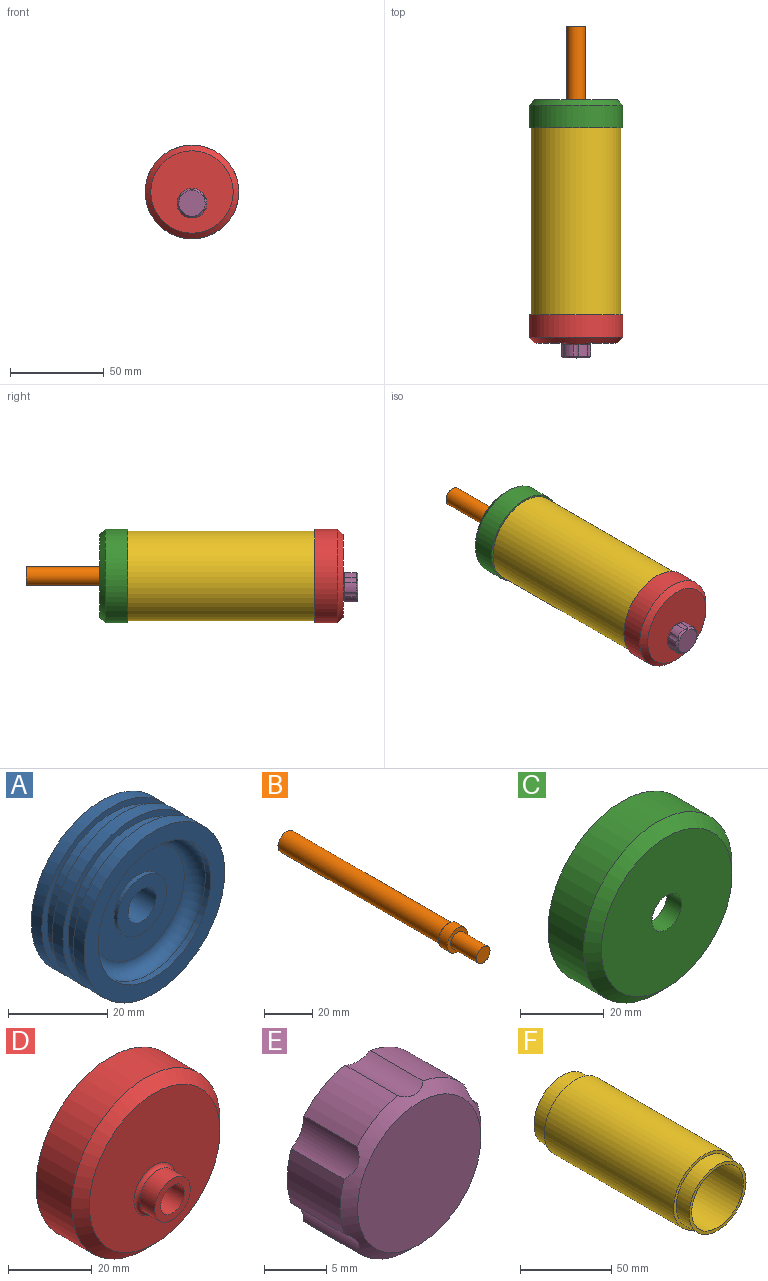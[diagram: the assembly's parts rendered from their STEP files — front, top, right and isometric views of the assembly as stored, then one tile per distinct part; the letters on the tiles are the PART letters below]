
ASSEMBLY  parts=6 mates=5
PART A: 22 faces, bbox 40x15.6x40 mm
  f0: cylinder r=20mm len=40mm, axis (0,1,0), area 377mm2, adj f6,f17
  f1: cylinder r=20mm len=40mm, axis (0,1,0), area 377mm2, adj f5,f15
  f2: cylinder r=7mm len=14mm, axis (0,1,0), area 44mm2, adj f3,f12
  f3: plane 26x26mm, normal (0,1,0), area 377mm2, adj f2,f20
  f4: cylinder r=16mm len=32mm, axis (0,1,0), area 150.8mm2, adj f5,f20
  f5: plane 40x40mm, normal (0,1,0), area 452.4mm2, adj f1,f4
  f6: plane 40x40mm, normal (0,-1,0), area 452.4mm2, adj f0,f7
  f7: cylinder r=16mm len=32mm, axis (0,1,0), area 150.8mm2, adj f6,f21
  f8: plane 26x26mm, normal (0,-1,0), area 377mm2, adj f9,f21
  f9: cylinder r=7mm len=14mm, axis (0,1,0), area 44mm2, adj f8,f10
  f10: plane 14x14mm, normal (0,-1,0), area 103.7mm2, adj f9,f11
  f11: cylinder r=4mm len=8mm, axis (0,1,0), area 201.1mm2, adj f10,f12
  f12: plane 14x14mm, normal (0,1,0), area 103.7mm2, adj f2,f11
  f13: plane 40x40mm, normal (0,1,0), area 181.4mm2, adj f14,f16
  f14: cylinder r=18.5mm len=37mm, axis (0,-1,0), area 348.7mm2, adj f13,f15
  f15: plane 40x40mm, normal (0,-1,0), area 181.4mm2, adj f1,f14
  f16: cylinder r=20mm len=40mm, axis (0,1,0), area 377mm2, adj f13,f19
  f17: plane 40x40mm, normal (0,1,0), area 181.4mm2, adj f0,f18
  f18: cylinder r=18.5mm len=37mm, axis (0,-1,0), area 348.7mm2, adj f17,f19
  f19: plane 40x40mm, normal (0,-1,0), area 181.4mm2, adj f16,f18
  f20: torus R=13mm, axis (0,1,0), area 441.5mm2, adj f3,f4
  f21: torus R=13mm, axis (0,1,0), area 441.5mm2, adj f7,f8
PART B: 7 faces, bbox 12x115x12 mm
  f0: plane 12x12mm, normal (0,-1,0), area 62.8mm2, adj f1,f3
  f1: cylinder r=4mm len=15mm, axis (0,1,0), area 377mm2, adj f0,f2
  f2: plane 8x8mm, normal (0,-1,0), area 50.3mm2, adj f1
  f3: cylinder r=6mm len=12mm, axis (0,-1,0), area 188.5mm2, adj f0,f6
  f4: plane 10x10mm, normal (0,1,0), area 78.5mm2, adj f5
  f5: cylinder r=5mm len=94mm, axis (0,1,0), area 2953.1mm2, adj f4,f6
  f6: cone r=6mm half-angle=45deg, axis (0,-1,0), area 48.9mm2, adj f3,f5
PART C: 7 faces, bbox 50x15x50 mm
  f0: plane 44x44mm, normal (0,-1,0), area 1442mm2, adj f1,f6
  f1: cylinder r=5mm len=10mm, axis (0,1,0), area 157.1mm2, adj f0,f2
  f2: plane 44x44mm, normal (0,1,0), area 1442mm2, adj f1,f3
  f3: cylinder r=22mm len=44mm, axis (0,1,0), area 1382.3mm2, adj f2,f4
  f4: plane 50x50mm, normal (0,1,0), area 443mm2, adj f3,f5
  f5: cylinder r=25mm len=50mm, axis (0,1,0), area 1885mm2, adj f4,f6
  f6: cone r=25mm half-angle=45deg, axis (0,1,0), area 626.4mm2, adj f0,f5
PART D: 10 faces, bbox 50x21x50 mm
  f0: plane 44x44mm, normal (0,1,0), area 1470.3mm2, adj f1,f8
  f1: cylinder r=22mm len=44mm, axis (0,1,0), area 1382.3mm2, adj f0,f2
  f2: plane 50x50mm, normal (0,1,0), area 443mm2, adj f1,f3
  f3: cylinder r=25mm len=50mm, axis (0,1,0), area 1885mm2, adj f2,f5
  f4: plane 44x44mm, normal (0,-1,0), area 1366.6mm2, adj f5,f9
  f5: cone r=25mm half-angle=45deg, axis (0,1,0), area 626.4mm2, adj f3,f4
  f6: cylinder r=6mm len=12mm, axis (0,1,0), area 188.5mm2, adj f7,f9
  f7: plane 12x12mm, normal (0,-1,0), area 62.8mm2, adj f6,f8
  f8: cylinder r=4mm len=11mm, axis (0,-1,0), area 276.5mm2, adj f0,f7
  f9: torus R=7mm, axis (0,1,0), area 62.8mm2, adj f4,f6
PART E: 17 faces, bbox 16x7x16 mm
  f0: cylinder r=8mm len=6mm, axis (0,1,0), area 32.9mm2, adj f7,f10,f11,f16
  f1: cylinder r=8mm len=6mm, axis (0,1,0), area 32.9mm2, adj f7,f10,f15,f16
  f2: cylinder r=8mm len=6mm, axis (0,1,0), area 32.9mm2, adj f7,f10,f14,f15
  f3: cylinder r=8mm len=6mm, axis (0,1,0), area 32.9mm2, adj f7,f10,f13,f14
  f4: cylinder r=8mm len=6mm, axis (0,1,0), area 32.9mm2, adj f7,f10,f12,f13
  f5: cylinder r=8mm len=6mm, axis (0,1,0), area 32.9mm2, adj f7,f10,f11,f12
  f6: plane 14x14mm, normal (0,-1,0), area 153.9mm2, adj f10
  f7: plane 16x15.74mm, normal (0,1,0), area 82.1mm2, adj f0,f1,f2,f3,f4,f5,f8,f11
  f8: cylinder r=6mm len=12mm, axis (0,1,0), area 188.5mm2, adj f7,f9
  f9: plane 12x12mm, normal (0,1,0), area 113.1mm2, adj f8
  f10: cone r=7mm half-angle=45deg, axis (0,1,0), area 58.4mm2, adj f0,f1,f2,f3,f4,f5,f6,f11
  f11: cylinder r=3mm len=6.5mm, axis (0,-1,0), area 19mm2, adj f0,f5,f7,f10
  f12: cylinder r=3mm len=6.5mm, axis (0,-1,0), area 19mm2, adj f4,f5,f7,f10
  f13: cylinder r=3mm len=6.5mm, axis (0,-1,0), area 19mm2, adj f3,f4,f7,f10
  f14: cylinder r=3mm len=6.5mm, axis (0,-1,0), area 19mm2, adj f2,f3,f7,f10
  f15: cylinder r=3mm len=6.5mm, axis (0,-1,0), area 19mm2, adj f1,f2,f7,f10
  f16: cylinder r=3mm len=6.5mm, axis (0,-1,0), area 19mm2, adj f0,f1,f7,f10
PART F: 8 faces, bbox 48x120x48 mm
  f0: cylinder r=22mm len=44mm, axis (0,1,0), area 1382.3mm2, adj f1,f7
  f1: plane 48x48mm, normal (0,1,0), area 289mm2, adj f0,f2
  f2: cylinder r=24mm len=100mm, axis (0,1,0), area 15079.6mm2, adj f1,f3
  f3: plane 48x48mm, normal (0,-1,0), area 289mm2, adj f2,f4
  f4: cylinder r=22mm len=44mm, axis (0,1,0), area 1382.3mm2, adj f3,f5
  f5: plane 44x44mm, normal (0,-1,0), area 263.9mm2, adj f4,f6
  f6: cylinder r=20mm len=120mm, axis (0,1,0), area 15079.6mm2, adj f5,f7
  f7: plane 44x44mm, normal (0,1,0), area 263.9mm2, adj f0,f6
PLACE A t=(-0.56,-10.42,-7.37)mm
PLACE B t=(-0.56,93.58,-7.37)mm
PLACE C rot(axis=(1,0,0),180deg) t=(-0.56,39.19,-7.37)mm
PLACE D t=(-0.56,-60.81,-7.37)mm
PLACE E t=(-0.56,-76.81,-13.37)mm
PLACE F t=(-0.56,49.19,-7.37)mm
MATE fastened D.f1 <-> F.f0  axis (0,1,0) through (-0.56,-70.81,-7.37)mm
MATE fastened E.f8 <-> D.f6  axis (0,1,0) through (-0.56,-81.81,-13.37)mm
MATE fastened A.f0 <-> B.f1  axis (0,1,0) through (-0.56,-6.42,-7.37)mm
MATE fastened C.f1 <-> F.f0  axis (0,-1,0) through (-0.56,49.19,-7.37)mm
MATE slider B.f5 <-> C.f1  axis (0,1,0) through (-0.56,46.58,-7.37)mm
